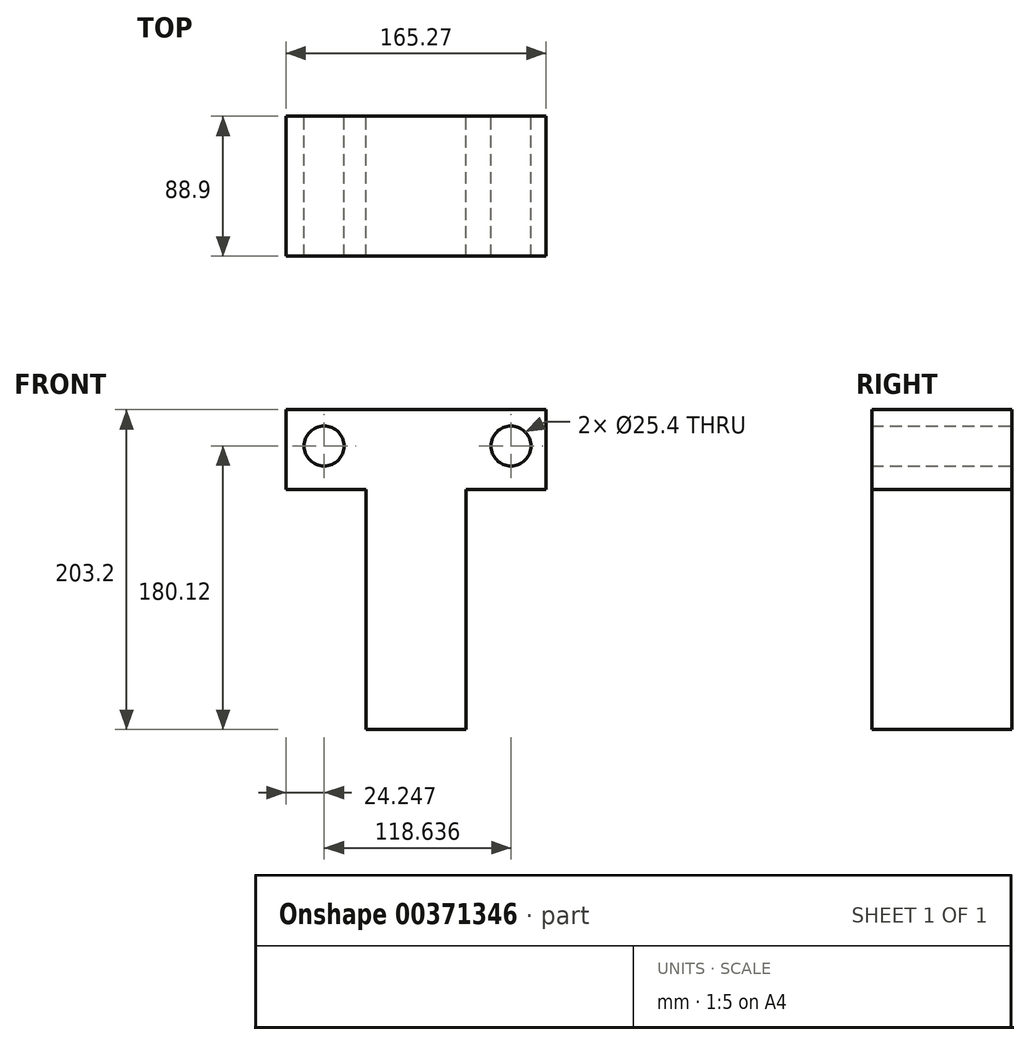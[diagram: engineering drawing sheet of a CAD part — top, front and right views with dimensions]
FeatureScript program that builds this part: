
annotation { "Feature Type Name" : "Feature", "Feature Type Description" : "" }
export const myFeature = defineFeature(function(context is Context, id is Id, definition is map)
    precondition{}
    {
        {
            var Q0;
            Q0=qCreatedBy(makeId("Front.planeOp"),FACE);
            var sketch = newSketch(context, id + "F0", { "sketchPlane" : qUnion([Q0])});
            skLineSegment(sketch, "E0.bottom", {"start": v(-31.75, 76.2) * mm, "end": v(31.75, 76.2) * mm});
            skLineSegment(sketch, "E0.top", {"start": v(-31.75, -76.2) * mm, "end": v(31.75, -76.2) * mm});
            skLineSegment(sketch, "E0.left", {"start": v(-31.75, 76.2) * mm, "end": v(-31.75, -76.2) * mm});
            skLineSegment(sketch, "E0.right", {"start": v(31.75, 76.2) * mm, "end": v(31.75, -76.2) * mm});
            skPoint(sketch, "E0.middle", {"position": v(0, 0) * mm});
            skLineSegment(sketch, "E1", {"start": v(-31.75, 76.2) * mm, "end": v(-82.55, 76.2) * mm});
            skLineSegment(sketch, "E2", {"start": v(31.75, 76.2) * mm, "end": v(82.55, 76.2) * mm});
            skLineSegment(sketch, "E3", {"start": v(-82.55, 76.2) * mm, "end": v(-82.55, 127) * mm});
            skLineSegment(sketch, "E4", {"start": v(-82.55, 127) * mm, "end": v(82.72, 127) * mm});
            skLineSegment(sketch, "E5", {"start": v(82.72, 127) * mm, "end": v(82.55, 76.2) * mm});
            skCircle(sketch, "E6", {"center": v(-58.3, 103.92) * mm, "radius": 12.7 * mm});
            skCircle(sketch, "E7", {"center": v(60.33, 103.92) * mm, "radius": 12.7 * mm});
            skSolve(sketch);
        }
        {
            var Q0;
            Q0 = qSketchRegion(id + "F0", true);
            var Q1;
            Q1=makeQuery(id+"F0.imprint","IMPRINT",FACE,{"disambiguationData":[TD([[makeQuery(id+"F0.imprint","IMPRINT",EDGE,{"derivedFrom":sQuery(id+"F0.wireOp",EDGE,"E0.bottom")}),1.0]])]});
            extrude(context, id + "F1", {"entities" : qUnion([Q0, Q1]), "depth" : 88.9 * mm});
        }
    });
